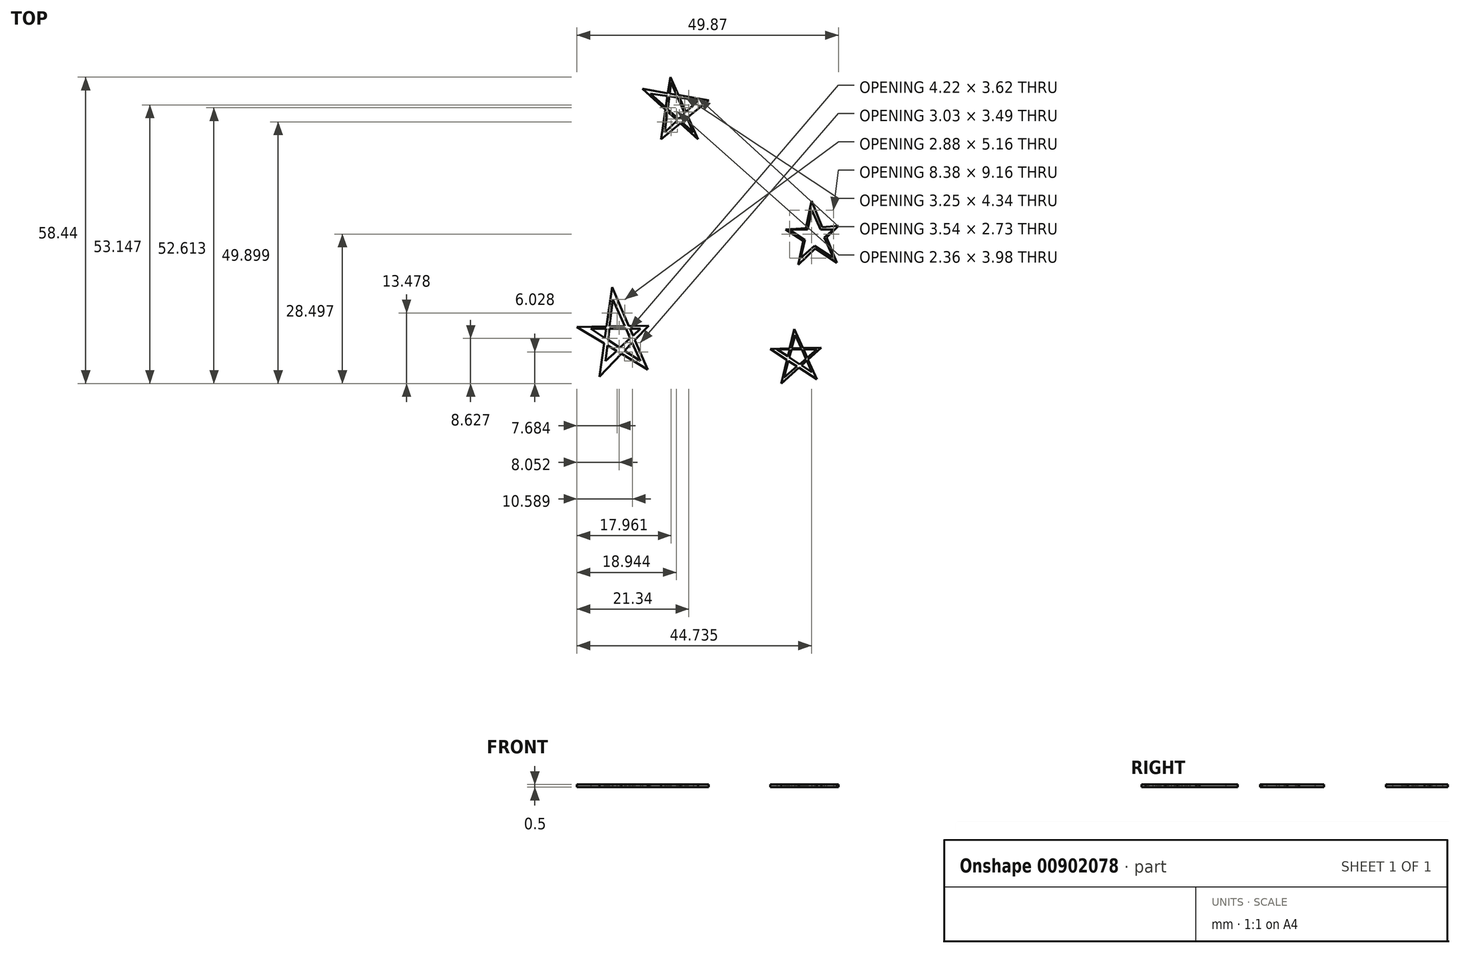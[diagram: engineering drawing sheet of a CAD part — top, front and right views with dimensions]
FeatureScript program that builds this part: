
annotation { "Feature Type Name" : "Feature", "Feature Type Description" : "" }
export const myFeature = defineFeature(function(context is Context, id is Id, definition is map)
    precondition{}
    {
        {
            var Q0;
            Q0=qCreatedBy(makeId("Top.planeOp"),FACE);
            var sketch = newSketch(context, id + "F0", { "sketchPlane" : qUnion([Q0])});
            skLineSegment(sketch, "E0", {"start": v(7.94, 17.02) * mm, "end": v(12.03, 7.86) * mm});
            skLineSegment(sketch, "E1", {"start": v(12.03, 7.86) * mm, "end": v(3.66, 13.31) * mm});
            skLineSegment(sketch, "E2", {"start": v(3.66, 13.31) * mm, "end": v(12.03, 13.31) * mm});
            skLineSegment(sketch, "E3", {"start": v(12.03, 13.31) * mm, "end": v(5.8, 7.86) * mm});
            skLineSegment(sketch, "E4", {"start": v(5.8, 7.86) * mm, "end": v(7.94, 17.02) * mm});
            skLineSegment(sketch, "E5", {"start": v(-30.05, 0) * mm, "end": v(-24.79, -11.78) * mm});
            skLineSegment(sketch, "E6", {"start": v(-24.79, -11.78) * mm, "end": v(-34.23, -5.62) * mm});
            skLineSegment(sketch, "E7", {"start": v(-34.23, -5.62) * mm, "end": v(-24.79, -5.62) * mm});
            skLineSegment(sketch, "E8", {"start": v(-24.79, -5.62) * mm, "end": v(-31.41, -11.78) * mm});
            skLineSegment(sketch, "E9", {"start": v(-31.41, -11.78) * mm, "end": v(-30.05, 0) * mm});
            skLineSegment(sketch, "E10", {"start": v(-18.94, 41.37) * mm, "end": v(-14.69, 31.85) * mm});
            skLineSegment(sketch, "E11", {"start": v(-14.69, 31.85) * mm, "end": v(-22.84, 39.23) * mm});
            skLineSegment(sketch, "E12", {"start": v(-22.84, 39.23) * mm, "end": v(-13.78, 37.96) * mm});
            skLineSegment(sketch, "E13", {"start": v(-13.78, 37.96) * mm, "end": v(-20.11, 31.85) * mm});
            skLineSegment(sketch, "E14", {"start": v(-20.11, 31.85) * mm, "end": v(-18.94, 41.37) * mm});
            skLineSegment(sketch, "E15", {"start": v(4.77, -6.8) * mm, "end": v(7.94, -13.9) * mm});
            skLineSegment(sketch, "E16", {"start": v(7.94, -13.9) * mm, "end": v(1.3, -9.57) * mm});
            skLineSegment(sketch, "E17", {"start": v(1.3, -9.57) * mm, "end": v(8.9, -9.57) * mm});
            skLineSegment(sketch, "E18", {"start": v(8.9, -9.57) * mm, "end": v(2.6, -14.94) * mm});
            skLineSegment(sketch, "E19", {"start": v(2.6, -14.94) * mm, "end": v(4.77, -6.8) * mm});
            skLineSegment(sketch, "E20", {"start": v(-13.78, -20.24) * mm, "end": v(-9.14, -28.5) * mm});
            skLineSegment(sketch, "E21", {"start": v(-9.14, -28.5) * mm, "end": v(-17.72, -24.1) * mm});
            skLineSegment(sketch, "E22", {"start": v(-17.72, -24.1) * mm, "end": v(-7.15, -23.17) * mm});
            skLineSegment(sketch, "E23", {"start": v(-7.15, -23.17) * mm, "end": v(-16.07, -28.18) * mm});
            skLineSegment(sketch, "E24", {"start": v(-16.07, -28.18) * mm, "end": v(-13.78, -20.24) * mm});
            skLineSegment(sketch, "E25", {"start": v(-19.07, 42.38) * mm, "end": v(-13.79, 30.55) * mm});
            skLineSegment(sketch, "E26", {"start": v(-13.79, 30.55) * mm, "end": v(-24.42, 40.17) * mm});
            skLineSegment(sketch, "E27", {"start": v(-24.42, 40.17) * mm, "end": v(-11.75, 37.96) * mm});
            skLineSegment(sketch, "E28", {"start": v(-11.75, 37.96) * mm, "end": v(-20.85, 30.55) * mm});
            skLineSegment(sketch, "E29", {"start": v(-20.85, 30.55) * mm, "end": v(-19.07, 42.38) * mm});
            skLineSegment(sketch, "E30", {"start": v(9.73, -9.2) * mm, "end": v(2.1, -16.06) * mm});
            skLineSegment(sketch, "E31", {"start": v(2.1, -16.06) * mm, "end": v(4.6, -5.64) * mm});
            skLineSegment(sketch, "E32", {"start": v(4.6, -5.64) * mm, "end": v(8.9, -15.27) * mm});
            skLineSegment(sketch, "E33", {"start": v(8.9, -15.27) * mm, "end": v(0, -9.48) * mm});
            skLineSegment(sketch, "E34", {"start": v(0, -9.48) * mm, "end": v(9.73, -9.2) * mm});
            skLineSegment(sketch, "E35", {"start": v(12.98, 14) * mm, "end": v(5.35, 6.57) * mm});
            skLineSegment(sketch, "E36", {"start": v(5.35, 6.57) * mm, "end": v(7.85, 18.76) * mm});
            skLineSegment(sketch, "E37", {"start": v(7.85, 18.76) * mm, "end": v(12.7, 6.97) * mm});
            skLineSegment(sketch, "E38", {"start": v(12.7, 6.97) * mm, "end": v(2.92, 13.35) * mm});
            skLineSegment(sketch, "E39", {"start": v(2.92, 13.35) * mm, "end": v(12.98, 14) * mm});
            skLineSegment(sketch, "E40", {"start": v(-23.18, -5.02) * mm, "end": v(-32.58, -14.72) * mm});
            skLineSegment(sketch, "E41", {"start": v(-32.58, -14.72) * mm, "end": v(-30.2, 2.33) * mm});
            skLineSegment(sketch, "E42", {"start": v(-30.2, 2.33) * mm, "end": v(-23.36, -13.4) * mm});
            skLineSegment(sketch, "E43", {"start": v(-23.36, -13.4) * mm, "end": v(-36.89, -5.29) * mm});
            skLineSegment(sketch, "E44", {"start": v(-36.89, -5.29) * mm, "end": v(-23.18, -5.02) * mm});
            skSolve(sketch);
        }
        {
            var Q0;
            {var subQ5=sQuery(id+"F0.wireOp",EDGE,"E12");var subQ6=sQuery(id+"F0.wireOp",EDGE,"E11");var subQ7=makeQuery(id+"F0.imprint","INTERSECT",VERTEX,{"derivedFrom":[subQ6,subQ5]});Q0=makeQuery(id+"F0.imprint","IMPRINT",FACE,{"disambiguationData":[TD([[makeQuery(id+"F0.imprint","IMPRINT",EDGE,{"disambiguationData":[TD([[subQ7,1.0]])],"derivedFrom":subQ6}),1.0]])]});}
            var Q1;
            {var subQ0=sQuery(id+"F0.wireOp",EDGE,"E29");var subQ1=sQuery(id+"F0.wireOp",EDGE,"E12");var subQ2=makeQuery(id+"F0.imprint","INTERSECT",VERTEX,{"derivedFrom":[subQ1,subQ0]});Q1=makeQuery(id+"F0.imprint","IMPRINT",FACE,{"disambiguationData":[TD([[makeQuery(id+"F0.imprint","IMPRINT",EDGE,{"disambiguationData":[TD([[subQ2,-1.0]])],"derivedFrom":subQ1}),1.0]])]});}
            var Q2;
            {var subQ3=sQuery(id+"F0.wireOp",EDGE,"E14");var subQ8=sQuery(id+"F0.wireOp",EDGE,"E10");var subQ9=makeQuery(id+"F0.imprint","INTERSECT",VERTEX,{"derivedFrom":[subQ8,subQ3]});Q2=makeQuery(id+"F0.imprint","IMPRINT",FACE,{"disambiguationData":[TD([[makeQuery(id+"F0.imprint","IMPRINT",EDGE,{"disambiguationData":[TD([[subQ9,-1.0]])],"derivedFrom":subQ8}),1.0]])]});}
            var Q3;
            {var subQ0=sQuery(id+"F0.wireOp",EDGE,"E27");var subQ1=sQuery(id+"F0.wireOp",EDGE,"E10");var subQ2=makeQuery(id+"F0.imprint","INTERSECT",VERTEX,{"derivedFrom":[subQ1,subQ0]});Q3=makeQuery(id+"F0.imprint","IMPRINT",FACE,{"disambiguationData":[TD([[makeQuery(id+"F0.imprint","IMPRINT",EDGE,{"disambiguationData":[TD([[subQ2,-1.0]])],"derivedFrom":subQ1}),1.0]])]});}
            var Q4;
            {var subQ0=sQuery(id+"F0.wireOp",EDGE,"E27");var subQ1=sQuery(id+"F0.wireOp",EDGE,"E10");var subQ2=makeQuery(id+"F0.imprint","INTERSECT",VERTEX,{"derivedFrom":[subQ1,subQ0]});Q4=makeQuery(id+"F0.imprint","IMPRINT",FACE,{"disambiguationData":[TD([[makeQuery(id+"F0.imprint","IMPRINT",EDGE,{"disambiguationData":[TD([[subQ2,-1.0]])],"derivedFrom":subQ1}),-1.0]])]});}
            var Q5;
            {var subQ3=sQuery(id+"F0.wireOp",EDGE,"E13");var subQ5=sQuery(id+"F0.wireOp",EDGE,"E12");var subQ6=makeQuery(id+"F0.imprint","INTERSECT",VERTEX,{"derivedFrom":[subQ5,subQ3]});Q5=makeQuery(id+"F0.imprint","IMPRINT",FACE,{"disambiguationData":[TD([[makeQuery(id+"F0.imprint","IMPRINT",EDGE,{"disambiguationData":[TD([[subQ6,1.0]])],"derivedFrom":subQ5}),1.0]])]});}
            var Q6;
            {var subQ0=sQuery(id+"F0.wireOp",EDGE,"E12");var subQ1=sQuery(id+"F0.wireOp",EDGE,"E10");var subQ2=makeQuery(id+"F0.imprint","INTERSECT",VERTEX,{"derivedFrom":[subQ1,subQ0]});Q6=makeQuery(id+"F0.imprint","IMPRINT",FACE,{"disambiguationData":[TD([[makeQuery(id+"F0.imprint","IMPRINT",EDGE,{"disambiguationData":[TD([[subQ2,-1.0]])],"derivedFrom":subQ1}),1.0]])]});}
            var Q7;
            {var subQ0=sQuery(id+"F0.wireOp",EDGE,"E13");var subQ1=sQuery(id+"F0.wireOp",EDGE,"E10");var subQ2=makeQuery(id+"F0.imprint","INTERSECT",VERTEX,{"derivedFrom":[subQ1,subQ0]});Q7=makeQuery(id+"F0.imprint","IMPRINT",FACE,{"disambiguationData":[TD([[makeQuery(id+"F0.imprint","IMPRINT",EDGE,{"disambiguationData":[TD([[subQ2,-1.0]])],"derivedFrom":subQ1}),1.0]])]});}
            var Q8;
            {var subQ5=sQuery(id+"F0.wireOp",EDGE,"E11");var subQ6=sQuery(id+"F0.wireOp",EDGE,"E10");var subQ7=makeQuery(id+"F0.imprint","INTERSECT",VERTEX,{"derivedFrom":[subQ6,subQ5]});Q8=makeQuery(id+"F0.imprint","IMPRINT",FACE,{"disambiguationData":[TD([[makeQuery(id+"F0.imprint","IMPRINT",EDGE,{"disambiguationData":[TD([[subQ7,1.0]])],"derivedFrom":subQ6}),1.0]])]});}
            var Q9;
            {var subQ0=sQuery(id+"F0.wireOp",EDGE,"E13");var subQ1=sQuery(id+"F0.wireOp",EDGE,"E10");var subQ2=makeQuery(id+"F0.imprint","INTERSECT",VERTEX,{"derivedFrom":[subQ1,subQ0]});Q9=makeQuery(id+"F0.imprint","IMPRINT",FACE,{"disambiguationData":[TD([[makeQuery(id+"F0.imprint","IMPRINT",EDGE,{"disambiguationData":[TD([[subQ2,-1.0]])],"derivedFrom":subQ1}),-1.0]])]});}
            var Q10;
            {var subQ3=sQuery(id+"F0.wireOp",EDGE,"E14");var subQ5=sQuery(id+"F0.wireOp",EDGE,"E13");var subQ6=makeQuery(id+"F0.imprint","INTERSECT",VERTEX,{"derivedFrom":[subQ5,subQ3]});Q10=makeQuery(id+"F0.imprint","IMPRINT",FACE,{"disambiguationData":[TD([[makeQuery(id+"F0.imprint","IMPRINT",EDGE,{"disambiguationData":[TD([[subQ6,1.0]])],"derivedFrom":subQ5}),1.0]])]});}
            var Q11;
            {var subQ0=sQuery(id+"F0.wireOp",EDGE,"E14");var subQ1=sQuery(id+"F0.wireOp",EDGE,"E11");var subQ2=makeQuery(id+"F0.imprint","INTERSECT",VERTEX,{"derivedFrom":[subQ1,subQ0]});Q11=makeQuery(id+"F0.imprint","IMPRINT",FACE,{"disambiguationData":[TD([[makeQuery(id+"F0.imprint","IMPRINT",EDGE,{"disambiguationData":[TD([[subQ2,-1.0]])],"derivedFrom":subQ1}),-1.0]])]});}
            var Q12;
            {var subQ0=sQuery(id+"F0.wireOp",EDGE,"E14");var subQ1=sQuery(id+"F0.wireOp",EDGE,"E11");var subQ2=makeQuery(id+"F0.imprint","INTERSECT",VERTEX,{"derivedFrom":[subQ1,subQ0]});Q12=makeQuery(id+"F0.imprint","IMPRINT",FACE,{"disambiguationData":[TD([[makeQuery(id+"F0.imprint","IMPRINT",EDGE,{"disambiguationData":[TD([[subQ2,-1.0]])],"derivedFrom":subQ1}),1.0]])]});}
            var Q13;
            {var subQ0=sQuery(id+"F0.wireOp",EDGE,"E13");var subQ1=sQuery(id+"F0.wireOp",EDGE,"E11");var subQ2=makeQuery(id+"F0.imprint","INTERSECT",VERTEX,{"derivedFrom":[subQ1,subQ0]});Q13=makeQuery(id+"F0.imprint","IMPRINT",FACE,{"disambiguationData":[TD([[makeQuery(id+"F0.imprint","IMPRINT",EDGE,{"disambiguationData":[TD([[subQ2,-1.0]])],"derivedFrom":subQ1}),1.0]])]});}
            var Q14;
            {var subQ0=sQuery(id+"F0.wireOp",EDGE,"E28");var subQ1=sQuery(id+"F0.wireOp",EDGE,"E11");var subQ2=makeQuery(id+"F0.imprint","INTERSECT",VERTEX,{"derivedFrom":[subQ1,subQ0]});Q14=makeQuery(id+"F0.imprint","IMPRINT",FACE,{"disambiguationData":[TD([[makeQuery(id+"F0.imprint","IMPRINT",EDGE,{"disambiguationData":[TD([[subQ2,-1.0]])],"derivedFrom":subQ1}),1.0]])]});}
            extrude(context, id + "F1", {"entities" : qUnion([Q0, Q1, Q2, Q3, Q4, Q5, Q6, Q7, Q8, Q9, Q10, Q11, Q12, Q13, Q14]), "depth" : .5 * mm, "offsetDistance" : 25 * mm});
        }
        {
            var Q0;
            {var subQ3=sQuery(id+"F0.wireOp",EDGE,"E17");var subQ8=sQuery(id+"F0.wireOp",EDGE,"E18");var subQ9=makeQuery(id+"F0.imprint","INTERSECT",VERTEX,{"derivedFrom":[subQ3,subQ8]});Q0=makeQuery(id+"F0.imprint","IMPRINT",FACE,{"disambiguationData":[TD([[makeQuery(id+"F0.imprint","IMPRINT",EDGE,{"disambiguationData":[TD([[subQ9,1.0]])],"derivedFrom":subQ3}),1.0]])]});}
            var Q1;
            {var subQ3=sQuery(id+"F0.wireOp",EDGE,"E16");var subQ8=sQuery(id+"F0.wireOp",EDGE,"E15");var subQ10=makeQuery(id+"F0.imprint","INTERSECT",VERTEX,{"derivedFrom":[subQ8,subQ3]});Q1=makeQuery(id+"F0.imprint","IMPRINT",FACE,{"disambiguationData":[TD([[makeQuery(id+"F0.imprint","IMPRINT",EDGE,{"disambiguationData":[TD([[subQ10,1.0]])],"derivedFrom":subQ8}),1.0]])]});}
            var Q2;
            {var subQ6=sQuery(id+"F0.wireOp",EDGE,"E18");var subQ8=sQuery(id+"F0.wireOp",EDGE,"E19");var subQ9=makeQuery(id+"F0.imprint","INTERSECT",VERTEX,{"derivedFrom":[subQ6,subQ8]});Q2=makeQuery(id+"F0.imprint","IMPRINT",FACE,{"disambiguationData":[TD([[makeQuery(id+"F0.imprint","IMPRINT",EDGE,{"disambiguationData":[TD([[subQ9,1.0]])],"derivedFrom":subQ6}),1.0]])]});}
            var Q3;
            {var subQ3=sQuery(id+"F0.wireOp",EDGE,"E17");var subQ8=sQuery(id+"F0.wireOp",EDGE,"E16");var subQ10=makeQuery(id+"F0.imprint","INTERSECT",VERTEX,{"derivedFrom":[subQ8,subQ3]});Q3=makeQuery(id+"F0.imprint","IMPRINT",FACE,{"disambiguationData":[TD([[makeQuery(id+"F0.imprint","IMPRINT",EDGE,{"disambiguationData":[TD([[subQ10,1.0]])],"derivedFrom":subQ8}),1.0]])]});}
            var Q4;
            {var subQ5=sQuery(id+"F0.wireOp",EDGE,"E19");var subQ6=sQuery(id+"F0.wireOp",EDGE,"E15");var subQ7=makeQuery(id+"F0.imprint","INTERSECT",VERTEX,{"derivedFrom":[subQ6,subQ5]});Q4=makeQuery(id+"F0.imprint","IMPRINT",FACE,{"disambiguationData":[TD([[makeQuery(id+"F0.imprint","IMPRINT",EDGE,{"disambiguationData":[TD([[subQ7,-1.0]])],"derivedFrom":subQ6}),1.0]])]});}
            var Q5;
            {var subQ0=sQuery(id+"F0.wireOp",EDGE,"E34");var subQ1=sQuery(id+"F0.wireOp",EDGE,"E15");var subQ2=makeQuery(id+"F0.imprint","INTERSECT",VERTEX,{"derivedFrom":[subQ1,subQ0]});Q5=makeQuery(id+"F0.imprint","IMPRINT",FACE,{"disambiguationData":[TD([[makeQuery(id+"F0.imprint","IMPRINT",EDGE,{"disambiguationData":[TD([[subQ2,-1.0]])],"derivedFrom":subQ1}),1.0]])]});}
            var Q6;
            {var subQ0=sQuery(id+"F0.wireOp",EDGE,"E31");var subQ1=sQuery(id+"F0.wireOp",EDGE,"E17");var subQ2=makeQuery(id+"F0.imprint","INTERSECT",VERTEX,{"derivedFrom":[subQ1,subQ0]});Q6=makeQuery(id+"F0.imprint","IMPRINT",FACE,{"disambiguationData":[TD([[makeQuery(id+"F0.imprint","IMPRINT",EDGE,{"disambiguationData":[TD([[subQ2,-1.0]])],"derivedFrom":subQ1}),1.0]])]});}
            var Q7;
            {var subQ0=sQuery(id+"F0.wireOp",EDGE,"E19");var subQ1=sQuery(id+"F0.wireOp",EDGE,"E16");var subQ2=makeQuery(id+"F0.imprint","INTERSECT",VERTEX,{"derivedFrom":[subQ1,subQ0]});Q7=makeQuery(id+"F0.imprint","IMPRINT",FACE,{"disambiguationData":[TD([[makeQuery(id+"F0.imprint","IMPRINT",EDGE,{"disambiguationData":[TD([[subQ2,-1.0]])],"derivedFrom":subQ1}),1.0]])]});}
            var Q8;
            {var subQ0=sQuery(id+"F0.wireOp",EDGE,"E30");var subQ1=sQuery(id+"F0.wireOp",EDGE,"E16");var subQ2=makeQuery(id+"F0.imprint","INTERSECT",VERTEX,{"derivedFrom":[subQ1,subQ0]});Q8=makeQuery(id+"F0.imprint","IMPRINT",FACE,{"disambiguationData":[TD([[makeQuery(id+"F0.imprint","IMPRINT",EDGE,{"disambiguationData":[TD([[subQ2,-1.0]])],"derivedFrom":subQ1}),1.0]])]});}
            var Q9;
            {var subQ0=sQuery(id+"F0.wireOp",EDGE,"E18");var subQ1=sQuery(id+"F0.wireOp",EDGE,"E15");var subQ2=makeQuery(id+"F0.imprint","INTERSECT",VERTEX,{"derivedFrom":[subQ1,subQ0]});Q9=makeQuery(id+"F0.imprint","IMPRINT",FACE,{"disambiguationData":[TD([[makeQuery(id+"F0.imprint","IMPRINT",EDGE,{"disambiguationData":[TD([[subQ2,-1.0]])],"derivedFrom":subQ1}),1.0]])]});}
            var Q10;
            {var subQ0=sQuery(id+"F0.wireOp",EDGE,"E17");var subQ1=sQuery(id+"F0.wireOp",EDGE,"E15");var subQ2=makeQuery(id+"F0.imprint","INTERSECT",VERTEX,{"derivedFrom":[subQ1,subQ0]});Q10=makeQuery(id+"F0.imprint","IMPRINT",FACE,{"disambiguationData":[TD([[makeQuery(id+"F0.imprint","IMPRINT",EDGE,{"disambiguationData":[TD([[subQ2,-1.0]])],"derivedFrom":subQ1}),1.0]])]});}
            var Q11;
            {var subQ0=sQuery(id+"F0.wireOp",EDGE,"E18");var subQ1=sQuery(id+"F0.wireOp",EDGE,"E15");var subQ2=makeQuery(id+"F0.imprint","INTERSECT",VERTEX,{"derivedFrom":[subQ1,subQ0]});Q11=makeQuery(id+"F0.imprint","IMPRINT",FACE,{"disambiguationData":[TD([[makeQuery(id+"F0.imprint","IMPRINT",EDGE,{"disambiguationData":[TD([[subQ2,-1.0]])],"derivedFrom":subQ1}),-1.0]])]});}
            var Q12;
            {var subQ0=sQuery(id+"F0.wireOp",EDGE,"E18");var subQ1=sQuery(id+"F0.wireOp",EDGE,"E16");var subQ2=makeQuery(id+"F0.imprint","INTERSECT",VERTEX,{"derivedFrom":[subQ1,subQ0]});Q12=makeQuery(id+"F0.imprint","IMPRINT",FACE,{"disambiguationData":[TD([[makeQuery(id+"F0.imprint","IMPRINT",EDGE,{"disambiguationData":[TD([[subQ2,-1.0]])],"derivedFrom":subQ1}),1.0]])]});}
            var Q13;
            {var subQ0=sQuery(id+"F0.wireOp",EDGE,"E19");var subQ1=sQuery(id+"F0.wireOp",EDGE,"E16");var subQ2=makeQuery(id+"F0.imprint","INTERSECT",VERTEX,{"derivedFrom":[subQ1,subQ0]});Q13=makeQuery(id+"F0.imprint","IMPRINT",FACE,{"disambiguationData":[TD([[makeQuery(id+"F0.imprint","IMPRINT",EDGE,{"disambiguationData":[TD([[subQ2,-1.0]])],"derivedFrom":subQ1}),-1.0]])]});}
            var Q14;
            {var subQ0=sQuery(id+"F0.wireOp",EDGE,"E34");var subQ1=sQuery(id+"F0.wireOp",EDGE,"E15");var subQ2=makeQuery(id+"F0.imprint","INTERSECT",VERTEX,{"derivedFrom":[subQ1,subQ0]});Q14=makeQuery(id+"F0.imprint","IMPRINT",FACE,{"disambiguationData":[TD([[makeQuery(id+"F0.imprint","IMPRINT",EDGE,{"disambiguationData":[TD([[subQ2,-1.0]])],"derivedFrom":subQ1}),-1.0]])]});}
            extrude(context, id + "F2", {"entities" : qUnion([Q0, Q1, Q2, Q3, Q4, Q5, Q6, Q7, Q8, Q9, Q10, Q11, Q12, Q13, Q14]), "depth" : .5 * mm, "offsetDistance" : 25 * mm});
        }
        {
            var Q0;
            {var subQ5=sQuery(id+"F0.wireOp",EDGE,"E4");var subQ6=sQuery(id+"F0.wireOp",EDGE,"E0");var subQ7=makeQuery(id+"F0.imprint","INTERSECT",VERTEX,{"derivedFrom":[subQ6,subQ5]});Q0=makeQuery(id+"F0.imprint","IMPRINT",FACE,{"disambiguationData":[TD([[makeQuery(id+"F0.imprint","IMPRINT",EDGE,{"disambiguationData":[TD([[subQ7,-1.0]])],"derivedFrom":subQ6}),1.0]])]});}
            var Q1;
            {var subQ0=sQuery(id+"F0.wireOp",EDGE,"E39");var subQ1=sQuery(id+"F0.wireOp",EDGE,"E0");var subQ2=makeQuery(id+"F0.imprint","INTERSECT",VERTEX,{"derivedFrom":[subQ1,subQ0]});Q1=makeQuery(id+"F0.imprint","IMPRINT",FACE,{"disambiguationData":[TD([[makeQuery(id+"F0.imprint","IMPRINT",EDGE,{"disambiguationData":[TD([[subQ2,-1.0]])],"derivedFrom":subQ1}),1.0]])]});}
            var Q2;
            {var subQ3=sQuery(id+"F0.wireOp",EDGE,"E2");var subQ8=sQuery(id+"F0.wireOp",EDGE,"E3");var subQ9=makeQuery(id+"F0.imprint","INTERSECT",VERTEX,{"derivedFrom":[subQ3,subQ8]});Q2=makeQuery(id+"F0.imprint","IMPRINT",FACE,{"disambiguationData":[TD([[makeQuery(id+"F0.imprint","IMPRINT",EDGE,{"disambiguationData":[TD([[subQ9,1.0]])],"derivedFrom":subQ3}),1.0]])]});}
            var Q3;
            {var subQ0=sQuery(id+"F0.wireOp",EDGE,"E3");var subQ1=sQuery(id+"F0.wireOp",EDGE,"E0");var subQ2=makeQuery(id+"F0.imprint","INTERSECT",VERTEX,{"derivedFrom":[subQ1,subQ0]});Q3=makeQuery(id+"F0.imprint","IMPRINT",FACE,{"disambiguationData":[TD([[makeQuery(id+"F0.imprint","IMPRINT",EDGE,{"disambiguationData":[TD([[subQ2,-1.0]])],"derivedFrom":subQ1}),1.0]])]});}
            var Q4;
            {var subQ3=sQuery(id+"F0.wireOp",EDGE,"E1");var subQ5=sQuery(id+"F0.wireOp",EDGE,"E0");var subQ6=makeQuery(id+"F0.imprint","INTERSECT",VERTEX,{"derivedFrom":[subQ5,subQ3]});Q4=makeQuery(id+"F0.imprint","IMPRINT",FACE,{"disambiguationData":[TD([[makeQuery(id+"F0.imprint","IMPRINT",EDGE,{"disambiguationData":[TD([[subQ6,1.0]])],"derivedFrom":subQ5}),1.0]])]});}
            var Q5;
            {var subQ0=sQuery(id+"F0.wireOp",EDGE,"E35");var subQ1=sQuery(id+"F0.wireOp",EDGE,"E1");var subQ2=makeQuery(id+"F0.imprint","INTERSECT",VERTEX,{"derivedFrom":[subQ1,subQ0]});Q5=makeQuery(id+"F0.imprint","IMPRINT",FACE,{"disambiguationData":[TD([[makeQuery(id+"F0.imprint","IMPRINT",EDGE,{"disambiguationData":[TD([[subQ2,-1.0]])],"derivedFrom":subQ1}),1.0]])]});}
            var Q6;
            {var subQ6=sQuery(id+"F0.wireOp",EDGE,"E3");var subQ8=sQuery(id+"F0.wireOp",EDGE,"E4");var subQ9=makeQuery(id+"F0.imprint","INTERSECT",VERTEX,{"derivedFrom":[subQ6,subQ8]});Q6=makeQuery(id+"F0.imprint","IMPRINT",FACE,{"disambiguationData":[TD([[makeQuery(id+"F0.imprint","IMPRINT",EDGE,{"disambiguationData":[TD([[subQ9,1.0]])],"derivedFrom":subQ6}),1.0]])]});}
            var Q7;
            {var subQ0=sQuery(id+"F0.wireOp",EDGE,"E4");var subQ1=sQuery(id+"F0.wireOp",EDGE,"E1");var subQ2=makeQuery(id+"F0.imprint","INTERSECT",VERTEX,{"derivedFrom":[subQ1,subQ0]});Q7=makeQuery(id+"F0.imprint","IMPRINT",FACE,{"disambiguationData":[TD([[makeQuery(id+"F0.imprint","IMPRINT",EDGE,{"disambiguationData":[TD([[subQ2,-1.0]])],"derivedFrom":subQ1}),1.0]])]});}
            var Q8;
            {var subQ3=sQuery(id+"F0.wireOp",EDGE,"E2");var subQ5=sQuery(id+"F0.wireOp",EDGE,"E1");var subQ6=makeQuery(id+"F0.imprint","INTERSECT",VERTEX,{"derivedFrom":[subQ5,subQ3]});Q8=makeQuery(id+"F0.imprint","IMPRINT",FACE,{"disambiguationData":[TD([[makeQuery(id+"F0.imprint","IMPRINT",EDGE,{"disambiguationData":[TD([[subQ6,1.0]])],"derivedFrom":subQ5}),1.0]])]});}
            var Q9;
            {var subQ0=sQuery(id+"F0.wireOp",EDGE,"E36");var subQ1=sQuery(id+"F0.wireOp",EDGE,"E2");var subQ2=makeQuery(id+"F0.imprint","INTERSECT",VERTEX,{"derivedFrom":[subQ1,subQ0]});Q9=makeQuery(id+"F0.imprint","IMPRINT",FACE,{"disambiguationData":[TD([[makeQuery(id+"F0.imprint","IMPRINT",EDGE,{"disambiguationData":[TD([[subQ2,-1.0]])],"derivedFrom":subQ1}),1.0]])]});}
            extrude(context, id + "F3", {"entities" : qUnion([Q0, Q1, Q2, Q3, Q4, Q5, Q6, Q7, Q8, Q9]), "depth" : .5 * mm, "offsetDistance" : 25 * mm});
        }
        {
            var Q0;
            {var subQ3=sQuery(id+"F0.wireOp",EDGE,"E7");var subQ8=sQuery(id+"F0.wireOp",EDGE,"E8");var subQ9=makeQuery(id+"F0.imprint","INTERSECT",VERTEX,{"derivedFrom":[subQ3,subQ8]});Q0=makeQuery(id+"F0.imprint","IMPRINT",FACE,{"disambiguationData":[TD([[makeQuery(id+"F0.imprint","IMPRINT",EDGE,{"disambiguationData":[TD([[subQ9,1.0]])],"derivedFrom":subQ3}),1.0]])]});}
            var Q1;
            {var subQ0=sQuery(id+"F0.wireOp",EDGE,"E8");var subQ1=sQuery(id+"F0.wireOp",EDGE,"E5");var subQ2=makeQuery(id+"F0.imprint","INTERSECT",VERTEX,{"derivedFrom":[subQ1,subQ0]});Q1=makeQuery(id+"F0.imprint","IMPRINT",FACE,{"disambiguationData":[TD([[makeQuery(id+"F0.imprint","IMPRINT",EDGE,{"disambiguationData":[TD([[subQ2,-1.0]])],"derivedFrom":subQ1}),1.0]])]});}
            var Q2;
            {var subQ0=sQuery(id+"F0.wireOp",EDGE,"E8");var subQ1=sQuery(id+"F0.wireOp",EDGE,"E5");var subQ2=makeQuery(id+"F0.imprint","INTERSECT",VERTEX,{"derivedFrom":[subQ1,subQ0]});Q2=makeQuery(id+"F0.imprint","IMPRINT",FACE,{"disambiguationData":[TD([[makeQuery(id+"F0.imprint","IMPRINT",EDGE,{"disambiguationData":[TD([[subQ2,-1.0]])],"derivedFrom":subQ1}),-1.0]])]});}
            var Q3;
            {var subQ0=sQuery(id+"F0.wireOp",EDGE,"E40");var subQ1=sQuery(id+"F0.wireOp",EDGE,"E6");var subQ2=makeQuery(id+"F0.imprint","INTERSECT",VERTEX,{"derivedFrom":[subQ1,subQ0]});Q3=makeQuery(id+"F0.imprint","IMPRINT",FACE,{"disambiguationData":[TD([[makeQuery(id+"F0.imprint","IMPRINT",EDGE,{"disambiguationData":[TD([[subQ2,-1.0]])],"derivedFrom":subQ1}),1.0]])]});}
            var Q4;
            {var subQ6=sQuery(id+"F0.wireOp",EDGE,"E8");var subQ8=sQuery(id+"F0.wireOp",EDGE,"E9");var subQ9=makeQuery(id+"F0.imprint","INTERSECT",VERTEX,{"derivedFrom":[subQ6,subQ8]});Q4=makeQuery(id+"F0.imprint","IMPRINT",FACE,{"disambiguationData":[TD([[makeQuery(id+"F0.imprint","IMPRINT",EDGE,{"disambiguationData":[TD([[subQ9,1.0]])],"derivedFrom":subQ6}),1.0]])]});}
            var Q5;
            {var subQ0=sQuery(id+"F0.wireOp",EDGE,"E8");var subQ1=sQuery(id+"F0.wireOp",EDGE,"E6");var subQ2=makeQuery(id+"F0.imprint","INTERSECT",VERTEX,{"derivedFrom":[subQ1,subQ0]});Q5=makeQuery(id+"F0.imprint","IMPRINT",FACE,{"disambiguationData":[TD([[makeQuery(id+"F0.imprint","IMPRINT",EDGE,{"disambiguationData":[TD([[subQ2,-1.0]])],"derivedFrom":subQ1}),1.0]])]});}
            var Q6;
            {var subQ0=sQuery(id+"F0.wireOp",EDGE,"E9");var subQ1=sQuery(id+"F0.wireOp",EDGE,"E6");var subQ2=makeQuery(id+"F0.imprint","INTERSECT",VERTEX,{"derivedFrom":[subQ1,subQ0]});Q6=makeQuery(id+"F0.imprint","IMPRINT",FACE,{"disambiguationData":[TD([[makeQuery(id+"F0.imprint","IMPRINT",EDGE,{"disambiguationData":[TD([[subQ2,-1.0]])],"derivedFrom":subQ1}),1.0]])]});}
            var Q7;
            {var subQ3=sQuery(id+"F0.wireOp",EDGE,"E7");var subQ8=sQuery(id+"F0.wireOp",EDGE,"E6");var subQ10=makeQuery(id+"F0.imprint","INTERSECT",VERTEX,{"derivedFrom":[subQ8,subQ3]});Q7=makeQuery(id+"F0.imprint","IMPRINT",FACE,{"disambiguationData":[TD([[makeQuery(id+"F0.imprint","IMPRINT",EDGE,{"disambiguationData":[TD([[subQ10,1.0]])],"derivedFrom":subQ8}),1.0]])]});}
            var Q8;
            {var subQ0=sQuery(id+"F0.wireOp",EDGE,"E9");var subQ1=sQuery(id+"F0.wireOp",EDGE,"E6");var subQ2=makeQuery(id+"F0.imprint","INTERSECT",VERTEX,{"derivedFrom":[subQ1,subQ0]});Q8=makeQuery(id+"F0.imprint","IMPRINT",FACE,{"disambiguationData":[TD([[makeQuery(id+"F0.imprint","IMPRINT",EDGE,{"disambiguationData":[TD([[subQ2,-1.0]])],"derivedFrom":subQ1}),-1.0]])]});}
            var Q9;
            {var subQ5=sQuery(id+"F0.wireOp",EDGE,"E9");var subQ6=sQuery(id+"F0.wireOp",EDGE,"E5");var subQ7=makeQuery(id+"F0.imprint","INTERSECT",VERTEX,{"derivedFrom":[subQ6,subQ5]});Q9=makeQuery(id+"F0.imprint","IMPRINT",FACE,{"disambiguationData":[TD([[makeQuery(id+"F0.imprint","IMPRINT",EDGE,{"disambiguationData":[TD([[subQ7,-1.0]])],"derivedFrom":subQ6}),1.0]])]});}
            var Q10;
            {var subQ3=sQuery(id+"F0.wireOp",EDGE,"E6");var subQ8=sQuery(id+"F0.wireOp",EDGE,"E5");var subQ10=makeQuery(id+"F0.imprint","INTERSECT",VERTEX,{"derivedFrom":[subQ8,subQ3]});Q10=makeQuery(id+"F0.imprint","IMPRINT",FACE,{"disambiguationData":[TD([[makeQuery(id+"F0.imprint","IMPRINT",EDGE,{"disambiguationData":[TD([[subQ10,1.0]])],"derivedFrom":subQ8}),1.0]])]});}
            var Q11;
            {var subQ0=sQuery(id+"F0.wireOp",EDGE,"E44");var subQ1=sQuery(id+"F0.wireOp",EDGE,"E5");var subQ2=makeQuery(id+"F0.imprint","INTERSECT",VERTEX,{"derivedFrom":[subQ1,subQ0]});Q11=makeQuery(id+"F0.imprint","IMPRINT",FACE,{"disambiguationData":[TD([[makeQuery(id+"F0.imprint","IMPRINT",EDGE,{"disambiguationData":[TD([[subQ2,-1.0]])],"derivedFrom":subQ1}),1.0]])]});}
            var Q12;
            {var subQ0=sQuery(id+"F0.wireOp",EDGE,"E7");var subQ1=sQuery(id+"F0.wireOp",EDGE,"E5");var subQ2=makeQuery(id+"F0.imprint","INTERSECT",VERTEX,{"derivedFrom":[subQ1,subQ0]});Q12=makeQuery(id+"F0.imprint","IMPRINT",FACE,{"disambiguationData":[TD([[makeQuery(id+"F0.imprint","IMPRINT",EDGE,{"disambiguationData":[TD([[subQ2,-1.0]])],"derivedFrom":subQ1}),1.0]])]});}
            var Q13;
            {var subQ0=sQuery(id+"F0.wireOp",EDGE,"E44");var subQ1=sQuery(id+"F0.wireOp",EDGE,"E5");var subQ2=makeQuery(id+"F0.imprint","INTERSECT",VERTEX,{"derivedFrom":[subQ1,subQ0]});Q13=makeQuery(id+"F0.imprint","IMPRINT",FACE,{"disambiguationData":[TD([[makeQuery(id+"F0.imprint","IMPRINT",EDGE,{"disambiguationData":[TD([[subQ2,-1.0]])],"derivedFrom":subQ1}),-1.0]])]});}
            var Q14;
            {var subQ0=sQuery(id+"F0.wireOp",EDGE,"E41");var subQ1=sQuery(id+"F0.wireOp",EDGE,"E7");var subQ2=makeQuery(id+"F0.imprint","INTERSECT",VERTEX,{"derivedFrom":[subQ1,subQ0]});Q14=makeQuery(id+"F0.imprint","IMPRINT",FACE,{"disambiguationData":[TD([[makeQuery(id+"F0.imprint","IMPRINT",EDGE,{"disambiguationData":[TD([[subQ2,-1.0]])],"derivedFrom":subQ1}),1.0]])]});}
            extrude(context, id + "F4", {"entities" : qUnion([Q0, Q1, Q2, Q3, Q4, Q5, Q6, Q7, Q8, Q9, Q10, Q11, Q12, Q13, Q14]), "depth" : .5 * mm, "offsetDistance" : 25 * mm});
        }
    });
